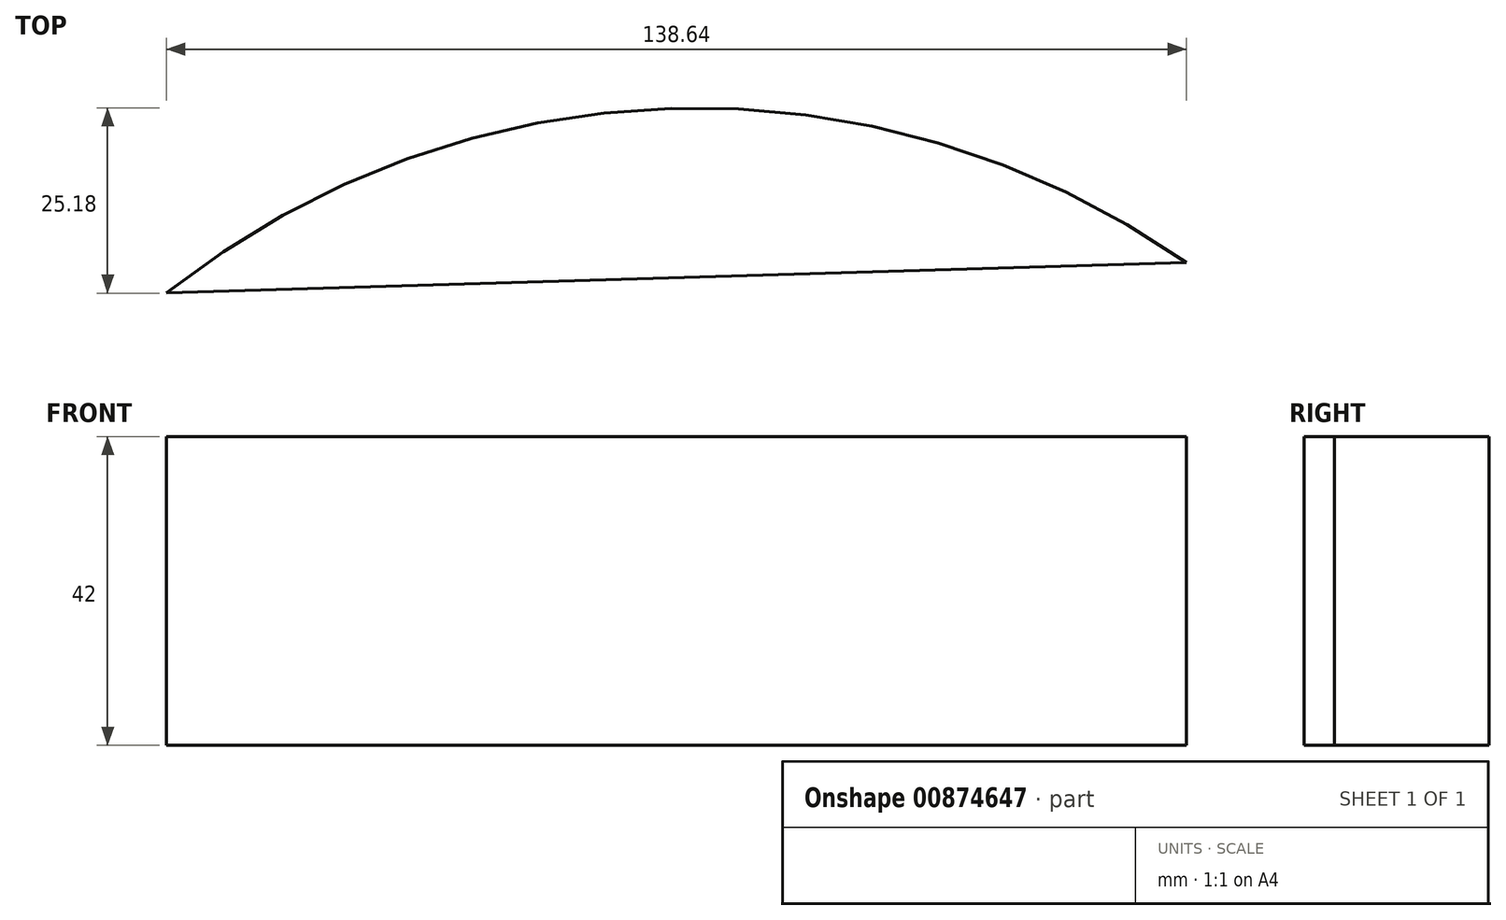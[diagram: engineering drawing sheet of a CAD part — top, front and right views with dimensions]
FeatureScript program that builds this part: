
annotation { "Feature Type Name" : "Feature", "Feature Type Description" : "" }
export const myFeature = defineFeature(function(context is Context, id is Id, definition is map)
    precondition{}
    {
        {
            var Q0;
            Q0=qCreatedBy(makeId("Top.planeOp"),FACE);
            var sketch = newSketch(context, id + "F0", { "sketchPlane" : qUnion([Q0])});
            skArc(sketch, "E0", {"start": v(62.93, 12.12) * mm, "mid": v(-7.08, 33.1) * mm, "end": v(-75.71, 7.98) * mm});
            skLineSegment(sketch, "E1", {"start": v(-75.71, 7.98) * mm, "end": v(62.93, 12.12) * mm});
            skSolve(sketch);
        }
        {
            var Q0;
            Q0 = qSketchRegion(id + "F0", true);
            extrude(context, id + "F1", {"entities" : qUnion([Q0]), "depth" : 42 * mm, "offsetDistance" : 25 * mm});
        }
    });
